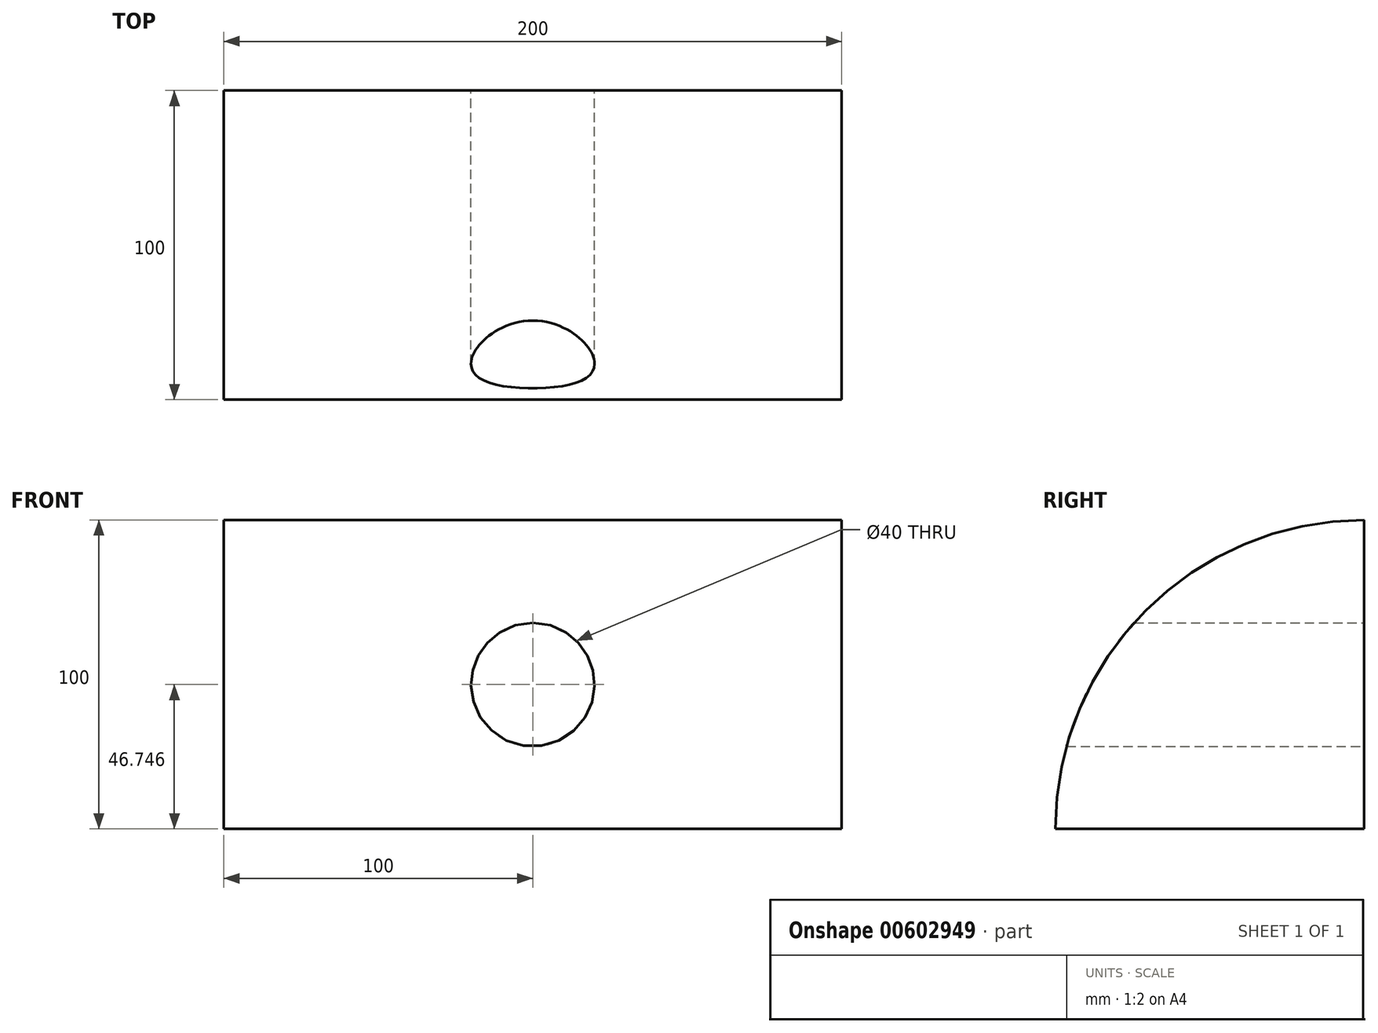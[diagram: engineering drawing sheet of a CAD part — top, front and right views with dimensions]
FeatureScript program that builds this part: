
annotation { "Feature Type Name" : "Feature", "Feature Type Description" : "" }
export const myFeature = defineFeature(function(context is Context, id is Id, definition is map)
    precondition{}
    {
        {
            var Q0;
            Q0=qCreatedBy(makeId("Front.planeOp"),FACE);
            var sketch = newSketch(context, id + "F0", { "sketchPlane" : qUnion([Q0])});
            skLineSegment(sketch, "E0.bottom", {"start": v(100, 50) * mm, "end": v(-100, 50) * mm});
            skLineSegment(sketch, "E0.top", {"start": v(100, -50) * mm, "end": v(-100, -50) * mm});
            skLineSegment(sketch, "E0.left", {"start": v(100, 50) * mm, "end": v(100, -50) * mm});
            skLineSegment(sketch, "E0.right", {"start": v(-100, 50) * mm, "end": v(-100, -50) * mm});
            skPoint(sketch, "E0.middle", {"position": v(0, 0) * mm});
            skCircle(sketch, "E1", {"center": v(0, -3.25) * mm, "radius": 20 * mm});
            skSolve(sketch);
        }
        {
            var Q0;
            Q0=makeQuery(id+"F0.imprint","IMPRINT",FACE,{"disambiguationData":[TD([[makeQuery(id+"F0.imprint","IMPRINT",EDGE,{"derivedFrom":sQuery(id+"F0.wireOp",EDGE,"E0.bottom")}),1.0]])]});
            extrude(context, id + "F1", {"entities" : qUnion([Q0]), "depth" : 100 * mm, "offsetDistance" : 25 * mm});
        }
        {
            var Q0;
            Q0=makeQuery(id+"F1.opExtrude","CAP_EDGE",EDGE,{"disambiguationData":[OSD([sQuery(id+"F0.wireOp",EDGE,"E0.bottom")])],"isStart":false});
            fillet(context, id + "F2", {"entities" : qUnion([Q0]), "radius" : 100 * mm, "tangentPropagation" : true, "allowEdgeOverflow" : false});
        }
    });
